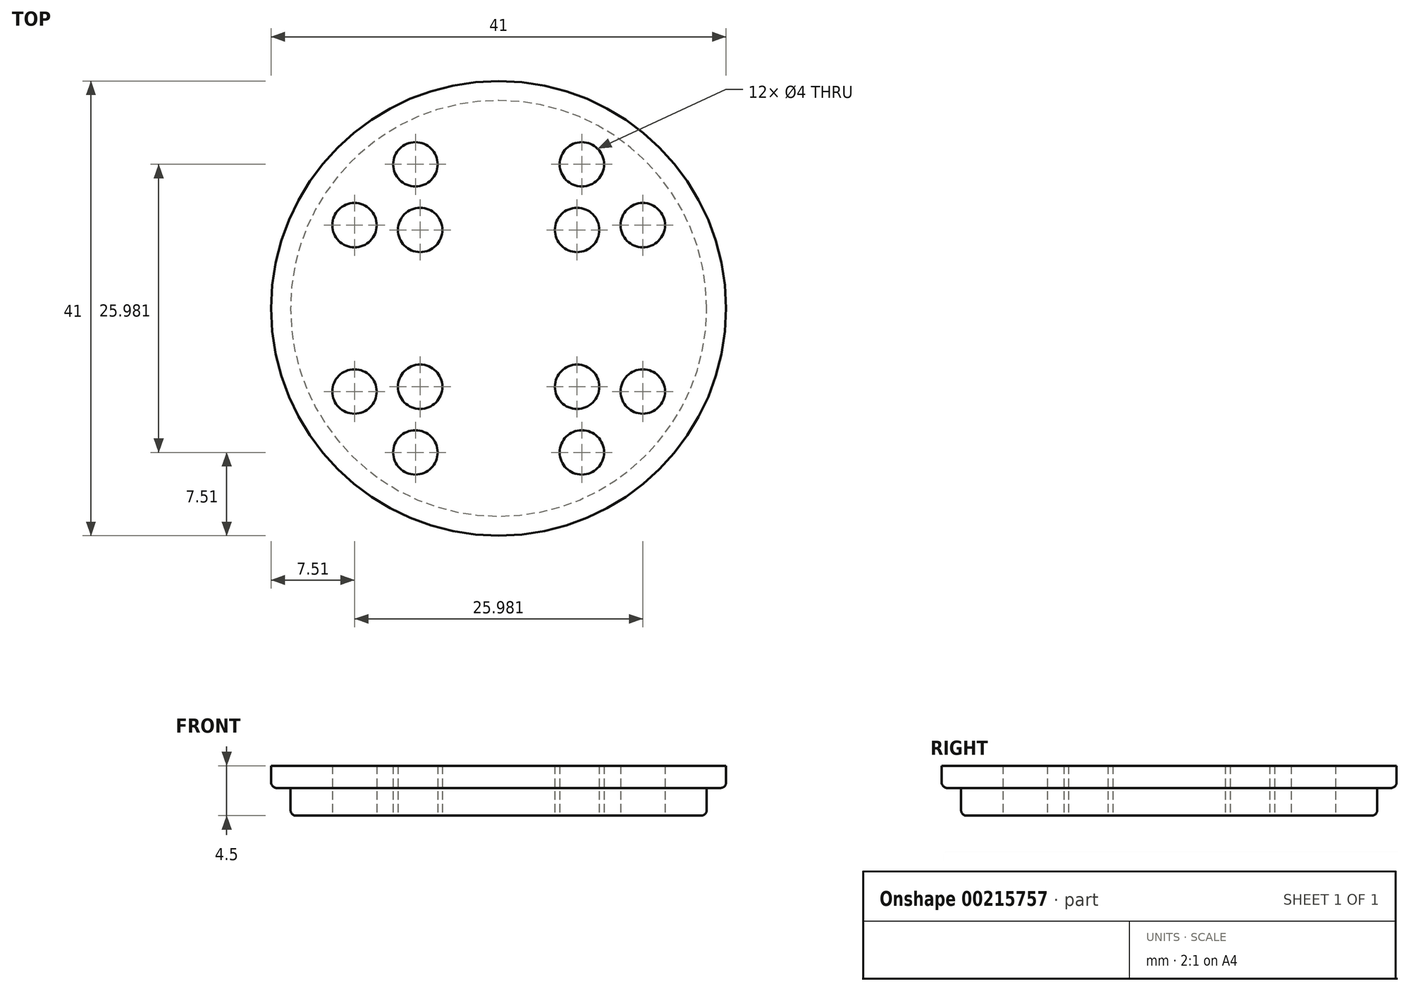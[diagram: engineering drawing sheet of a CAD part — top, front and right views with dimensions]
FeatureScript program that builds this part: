
annotation { "Feature Type Name" : "Feature", "Feature Type Description" : "" }
export const myFeature = defineFeature(function(context is Context, id is Id, definition is map)
    precondition{}
    {
        {
            var Q0;
            Q0=qCreatedBy(makeId("Top.planeOp"),FACE);
            var sketch = newSketch(context, id + "F0", { "sketchPlane" : qUnion([Q0])});
            skCircle(sketch, "E0", {"center": v(0, 0) * mm, "radius": 18.75 * mm});
            skSolve(sketch);
        }
        {
            var Q0;
            Q0=qSketchRegion(id+"F0",true);
            extrude(context, id + "F1", {"entities" : qUnion([Q0]), "depth" : 2.5 * mm});
        }
        {
            var Q0;
            Q0=makeQuery(id+"F1.opExtrude","CAP_FACE",FACE,{"disambiguationData":[OSD([sQuery(id+"F0.wireOp",EDGE,"E0")])],"isStart":false});
            var sketch = newSketch(context, id + "F2", { "sketchPlane" : qUnion([Q0])});
            skLineSegment(sketch, "E1", {"start": v(0, 0) * mm, "end": v(0, 18.75) * mm});
            skLineSegment(sketch, "E2", {"start": v(0, 0) * mm, "end": v(0, -18.75) * mm});
            skPoint(sketch, "E2.endSnap0", {"position": v(0, -1) * mm});
            skLineSegment(sketch, "E3", {"start": v(0, 0) * mm, "end": v(-18.75, 0) * mm});
            skLineSegment(sketch, "E4", {"start": v(0, 0) * mm, "end": v(18.75, 0) * mm});
            skCircle(sketch, "E5", {"center": v(0, 0) * mm, "radius": 10 * mm});
            skCircle(sketch, "E6", {"center": v(0, 0) * mm, "radius": 15 * mm});
            skLineSegment(sketch, "E7", {"start": v(0, 0) * mm, "end": v(-20.9, 12.07) * mm});
            skLineSegment(sketch, "E8", {"start": v(0, 0) * mm, "end": v(-17, 17) * mm});
            skLineSegment(sketch, "E9", {"start": v(0, 0) * mm, "end": v(-10.5, 18.2) * mm});
            skPoint(sketch, "E10", {"position": v(-13, 7.5) * mm});
            skPoint(sketch, "E11", {"position": v(-7.5, 13) * mm});
            skPoint(sketch, "E12", {"position": v(-7.07, 7.07) * mm});
            skPoint(sketch, "E13.MirrorP", {"position": v(13, 7.5) * mm});
            skPoint(sketch, "E14.MirrorP", {"position": v(7.07, 7.07) * mm});
            skPoint(sketch, "E15.MirrorP", {"position": v(7.5, 13) * mm});
            skPoint(sketch, "E16.MirrorP", {"position": v(-13, -7.5) * mm});
            skPoint(sketch, "E17.MirrorP", {"position": v(-7.07, -7.07) * mm});
            skPoint(sketch, "E18.MirrorP", {"position": v(-7.5, -13) * mm});
            skPoint(sketch, "E19.MirrorP", {"position": v(7.5, -13) * mm});
            skPoint(sketch, "E20.MirrorP", {"position": v(7.07, -7.07) * mm});
            skPoint(sketch, "E21.MirrorP", {"position": v(13, -7.5) * mm});
            skSolve(sketch);
        }
        {
            var Q0;
            Q0=makeQuery(id+"F1.opExtrude","CAP_EDGE",EDGE,{"disambiguationData":[OSD([sQuery(id+"F0.wireOp",EDGE,"E0")])],"isStart":true});
            fillet(context, id + "F3", {"entities" : qUnion([Q0]), "radius" : 0.5 * mm, "tangentPropagation" : true, "allowEdgeOverflow" : false});
        }
        {
            var Q0;
            Q0=makeQuery(id+"F1.opExtrude","CAP_FACE",FACE,{"disambiguationData":[OSD([sQuery(id+"F0.wireOp",EDGE,"E0")])],"isStart":false});
            var sketch = newSketch(context, id + "F4", { "sketchPlane" : qUnion([Q0])});
            skCircle(sketch, "E22", {"center": v(0, 0) * mm, "radius": 20.5 * mm});
            skSolve(sketch);
        }
        {
            var Q0;
            Q0 = qSketchRegion(id + "F4", true);
            extrude(context, id + "F5", {"entities" : qUnion([Q0]), "operationType" : NewBodyOperationType.ADD, "depth" : 2 * mm});
        }
        {
            var Q0;
            Q0=sQuery(id+"F2.wireOp",VERTEX,"E18.MirrorP");
            var Q1;
            Q1=sQuery(id+"F2.wireOp",VERTEX,"E16.MirrorP");
            var Q2;
            Q2=sQuery(id+"F2.wireOp",VERTEX,"E17.MirrorP");
            var Q3;
            Q3=sQuery(id+"F2.wireOp",VERTEX,"E10");
            var Q4;
            Q4=sQuery(id+"F2.wireOp",VERTEX,"E12");
            var Q5;
            Q5=sQuery(id+"F2.wireOp",VERTEX,"E11");
            var Q6;
            Q6=sQuery(id+"F2.wireOp",VERTEX,"E15.MirrorP");
            var Q7;
            Q7=sQuery(id+"F2.wireOp",VERTEX,"E14.MirrorP");
            var Q8;
            Q8=sQuery(id+"F2.wireOp",VERTEX,"E13.MirrorP");
            var Q9;
            Q9=sQuery(id+"F2.wireOp",VERTEX,"E20.MirrorP");
            var Q10;
            Q10=sQuery(id+"F2.wireOp",VERTEX,"E19.MirrorP");
            var Q11;
            Q11=sQuery(id+"F2.wireOp",VERTEX,"E21.MirrorP");
            var Q12;
            Q12=makeQuery(id+"F1.opExtrude","SWEPT_BODY",BODY,{"disambiguationData":[OSD([sQuery(id+"F0.wireOp",EDGE,"E0")])]});
            hole(context, id + "F6", {"style" : HoleStyle.SIMPLE, "endStyle" : HoleEndStyle.THROUGH, "oppositeDirection" : true, "holeDiameter" : 4 * mm, "locations" : qUnion([Q0, Q1, Q2, Q3, Q4, Q5, Q6, Q7, Q8, Q9, Q10, Q11]), "scope" : qUnion([Q12]), "isTappedThrough" : true});
        }
        {
            var Q0;
            Q0=sQuery(id+"F2.wireOp",VERTEX,"E10");
            var Q1;
            Q1=sQuery(id+"F2.wireOp",VERTEX,"E11");
            var Q2;
            Q2=sQuery(id+"F2.wireOp",VERTEX,"E12");
            var Q3;
            Q3=sQuery(id+"F2.wireOp",VERTEX,"E16.MirrorP");
            var Q4;
            Q4=sQuery(id+"F2.wireOp",VERTEX,"E17.MirrorP");
            var Q5;
            Q5=sQuery(id+"F2.wireOp",VERTEX,"E18.MirrorP");
            var Q6;
            Q6=sQuery(id+"F2.wireOp",VERTEX,"E19.MirrorP");
            var Q7;
            Q7=sQuery(id+"F2.wireOp",VERTEX,"E20.MirrorP");
            var Q8;
            Q8=sQuery(id+"F2.wireOp",VERTEX,"E21.MirrorP");
            var Q9;
            Q9=sQuery(id+"F2.wireOp",VERTEX,"E14.MirrorP");
            var Q10;
            Q10=sQuery(id+"F2.wireOp",VERTEX,"E13.MirrorP");
            var Q11;
            Q11=sQuery(id+"F2.wireOp",VERTEX,"E15.MirrorP");
            var Q12;
            Q12=makeQuery(id+"F1.opExtrude","SWEPT_BODY",BODY,{"disambiguationData":[OSD([sQuery(id+"F0.wireOp",EDGE,"E0")])]});
            hole(context, id + "F7", {"style" : HoleStyle.SIMPLE, "endStyle" : HoleEndStyle.THROUGH, "holeDiameter" : 4 * mm, "locations" : qUnion([Q0, Q1, Q2, Q3, Q4, Q5, Q6, Q7, Q8, Q9, Q10, Q11]), "scope" : qUnion([Q12]), "isTappedThrough" : true});
        }
        {
            var Q0;
            Q0=makeQuery(id+"F5.opExtrude","CAP_EDGE",EDGE,{"disambiguationData":[OSD([sQuery(id+"F4.wireOp",EDGE,"E22")])],"isStart":true});
            fillet(context, id + "F8", {"entities" : qUnion([Q0]), "radius" : 0.5 * mm, "tangentPropagation" : true, "allowEdgeOverflow" : false});
        }
    });
